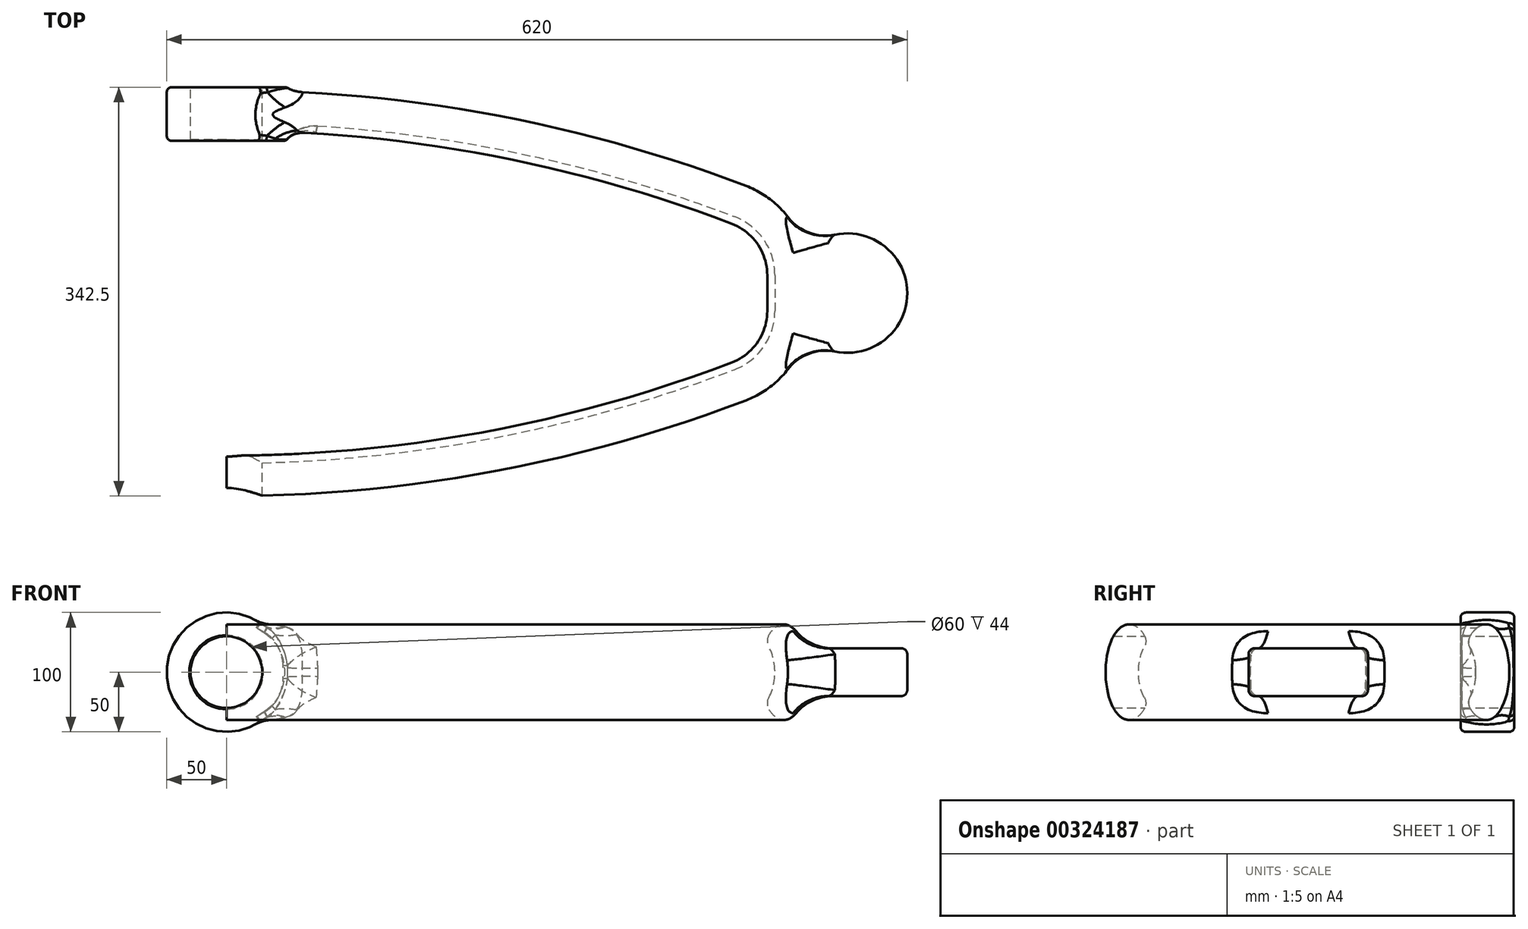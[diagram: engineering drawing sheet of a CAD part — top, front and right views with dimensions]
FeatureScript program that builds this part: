
annotation { "Feature Type Name" : "Feature", "Feature Type Description" : "" }
export const myFeature = defineFeature(function(context is Context, id is Id, definition is map)
    precondition{}
    {
        {
            var Q0;
            Q0=qCreatedBy(makeId("Top.planeOp"),FACE);
            var sketch = newSketch(context, id + "F0", { "sketchPlane" : qUnion([Q0])});
            skArc(sketch, "E0", {"start": v(28.07, 71.05) * mm, "mid": v(-182.36, 130.1) * mm, "end": v(-400, 150) * mm});
            skArc(sketch, "E1", {"start": v(66.66, 15) * mm, "mid": v(56.08, 49.03) * mm, "end": v(28.07, 71.05) * mm});
            skLineSegment(sketch, "E2", {"start": v(0, 0) * mm, "end": v(-439.5, 0) * mm, "construction": true});
            skLineSegment(sketch, "E3", {"start": v(-400, 150) * mm, "end": v(-513.06, 150) * mm, "construction": true});
            skLineSegment(sketch, "E4", {"start": v(-470.76, -150) * mm, "end": v(-400, -150) * mm, "construction": true});
            skArc(sketch, "E5", {"start": v(-400, -150) * mm, "mid": v(-182.36, -130.1) * mm, "end": v(28.07, -71.05) * mm});
            skArc(sketch, "E6", {"start": v(28.07, -71.05) * mm, "mid": v(56.08, -49.03) * mm, "end": v(66.66, -15) * mm});
            skLineSegment(sketch, "E7", {"start": v(66.66, 15) * mm, "end": v(66.66, -15) * mm});
            skLineSegment(sketch, "E8", {"start": v(66.66, 0) * mm, "end": v(0, 0) * mm});
            skSolve(sketch);
        }
        {
            var Q0;
            Q0=qCreatedBy(makeId("Right.planeOp"),FACE);
            var Q1;
            Q1=sQuery(id+"F0.wireOp",VERTEX,"E3.start");
            cPlane(context, id + "F1", {"entities" : qUnion([Q0, Q1]), "cplaneType" : CPlaneType.PLANE_POINT, "offset" : 25 * mm, "width" : 150 * mm, "height" : 150 * mm});
        }
        {
            var Q0;
            Q0=qCreatedBy(id+"F1.planeOp",FACE);
            var sketch = newSketch(context, id + "F2", { "sketchPlane" : qUnion([Q0])});
            skEllipse(sketch, "E9", {"center": v(150, 0) * mm, "majorRadius": 40 * mm, "minorRadius": 20 * mm, "majorAxis": v(0, 1)});
            skSolve(sketch);
        }
        {
            var Q0;
            Q0=makeQuery(id+"F2.imprint","IMPRINT",FACE,{"disambiguationData":[TD([[makeQuery(id+"F2.imprint","IMPRINT",EDGE,{"derivedFrom":sQuery(id+"F2.wireOp",EDGE,"E9")}),1.0]])]});
            var Q1;
            Q1=sQuery(id+"F0.wireOp",EDGE,"E0");
            var Q2;
            Q2=sQuery(id+"F0.wireOp",EDGE,"E1");
            var Q3;
            Q3=sQuery(id+"F0.wireOp",EDGE,"E7");
            var Q4;
            Q4=sQuery(id+"F0.wireOp",EDGE,"E6");
            var Q5;
            Q5=sQuery(id+"F0.wireOp",EDGE,"E5");
            sweep(context, id + "F3", {"profiles" : qUnion([Q0]), "path" : qUnion([Q1, Q2, Q3, Q4, Q5])});
        }
        {
            var Q0;
            Q0=qCreatedBy(id+"F1.planeOp",FACE);
            var sketch = newSketch(context, id + "F4", { "sketchPlane" : qUnion([Q0])});
            skEllipse(sketch, "E10", {"center": v(125, 0) * mm, "majorRadius": 30 * mm, "minorRadius": 17.5 * mm, "majorAxis": v(0, -1)});
            skSolve(sketch);
        }
        {
            var Q0;
            Q0=makeQuery(id+"F4.imprint","IMPRINT",FACE,{"disambiguationData":[TD([[makeQuery(id+"F4.imprint","IMPRINT",EDGE,{"derivedFrom":sQuery(id+"F4.wireOp",EDGE,"E10")}),1.0]])]});
            var Q1;
            Q1=sQuery(id+"F0.wireOp",EDGE,"E0");
            var Q2;
            Q2=sQuery(id+"F0.wireOp",EDGE,"E1");
            var Q3;
            Q3=sQuery(id+"F0.wireOp",EDGE,"E7");
            var Q4;
            Q4=sQuery(id+"F0.wireOp",EDGE,"E6");
            var Q5;
            Q5=sQuery(id+"F0.wireOp",EDGE,"E5");
            sweep(context, id + "F5", {"operationType" : NewBodyOperationType.REMOVE, "profiles" : qUnion([Q0]), "path" : qUnion([Q1, Q2, Q3, Q4, Q5])});
        }
        {
            var Q0;
            {var subQ0=sQuery(id+"F0.wireOp",EDGE,"E0");Q0=makeQuery(id+"F5.boolean.opBoolean","INTERSECT",EDGE,{"disambiguationData":[OD(0.0)],"derivedFrom":[makeQuery(id+"F3.opSweep","SWEPT_FACE",FACE,{"disambiguationData":[OSD([subQ0,sQuery(id+"F2.wireOp",EDGE,"E9")])]}),makeQuery(id+"F5.opSweep","SWEPT_FACE",FACE,{"disambiguationData":[OSD([subQ0,sQuery(id+"F4.wireOp",EDGE,"E10")])]})]});}
            var Q1;
            {var subQ0=sQuery(id+"F0.wireOp",EDGE,"E0");Q1=makeQuery(id+"F5.boolean.opBoolean","INTERSECT",EDGE,{"disambiguationData":[OD(1.0)],"derivedFrom":[makeQuery(id+"F3.opSweep","SWEPT_FACE",FACE,{"disambiguationData":[OSD([subQ0,sQuery(id+"F2.wireOp",EDGE,"E9")])]}),makeQuery(id+"F5.opSweep","SWEPT_FACE",FACE,{"disambiguationData":[OSD([subQ0,sQuery(id+"F4.wireOp",EDGE,"E10")])]})]});}
            fillet(context, id + "F6", {"entities" : qUnion([Q0, Q1]), "radius" : 10 * mm, "tangentPropagation" : true, "allowEdgeOverflow" : false});
        }
        {
            var Q0;
            Q0=sQuery(id+"F2.wireOp",VERTEX,"E9.center");
            var Q1;
            Q1=qCreatedBy(makeId("Front.planeOp"),FACE);
            cPlane(context, id + "F7", {"entities" : qUnion([Q0, Q1]), "cplaneType" : CPlaneType.PLANE_POINT, "offset" : 25 * mm, "width" : 150 * mm, "height" : 150 * mm});
        }
        {
            var Q0;
            Q0=qCreatedBy(id+"F7.planeOp",FACE);
            var sketch = newSketch(context, id + "F8", { "sketchPlane" : qUnion([Q0])});
            skCircle(sketch, "E11", {"center": v(-400, 0) * mm, "radius": 50 * mm});
            skSolve(sketch);
        }
        {
            var Q0;
            Q0=makeQuery(id+"F8.imprint","IMPRINT",FACE,{"disambiguationData":[TD([[makeQuery(id+"F8.imprint","IMPRINT",EDGE,{"derivedFrom":sQuery(id+"F8.wireOp",EDGE,"E11")}),1.0]])]});
            extrude(context, id + "F9", {"entities" : qUnion([Q0]), "operationType" : NewBodyOperationType.ADD, "depth" : 45 * mm, "symmetric" : true});
        }
        {
            var Q0;
            Q0=makeQuery(id+"F9.boolean.opBoolean","INTERSECT",EDGE,{"derivedFrom":[makeQuery(id+"F3.opSweep","SWEPT_FACE",FACE,{"disambiguationData":[OSD([sQuery(id+"F0.wireOp",EDGE,"E0"),sQuery(id+"F2.wireOp",EDGE,"E9")])]}),makeQuery(id+"F9.opExtrude","SWEPT_FACE",FACE,{"disambiguationData":[OSD([sQuery(id+"F8.wireOp",EDGE,"E11")])]})]});
            fillet(context, id + "F10", {"entities" : qUnion([Q0]), "radius" : 30 * mm, "tangentPropagation" : true, "allowEdgeOverflow" : false});
        }
        {
            var Q0;
            {var subQ0=sQuery(id+"F8.wireOp",EDGE,"E11");Q0=makeQuery(id+"F10.opFillet","BLEND_EDGE",EDGE,{"disambiguationData":[OD(0.0)],"blendedFrom":[makeQuery(id+"F9.boolean.opBoolean","INTERSECT",EDGE,{"derivedFrom":[makeQuery(id+"F3.opSweep","SWEPT_FACE",FACE,{"disambiguationData":[OSD([sQuery(id+"F0.wireOp",EDGE,"E0"),sQuery(id+"F2.wireOp",EDGE,"E9")])]}),makeQuery(id+"F9.opExtrude","SWEPT_FACE",FACE,{"disambiguationData":[OSD([subQ0])]})]}),makeQuery(id+"F9.opExtrude","CAP_FACE",FACE,{"disambiguationData":[OSD([subQ0])],"isStart":false})],"blendedInto":[makeQuery(id+"F9.opExtrude","CAP_FACE",FACE,{"disambiguationData":[OSD([subQ0])],"isStart":false})]});}
            var Q1;
            {var subQ0=sQuery(id+"F8.wireOp",EDGE,"E11");Q1=makeQuery(id+"F10.opFillet","BLEND_EDGE",EDGE,{"blendedFrom":[makeQuery(id+"F9.boolean.opBoolean","INTERSECT",EDGE,{"derivedFrom":[makeQuery(id+"F3.opSweep","SWEPT_FACE",FACE,{"disambiguationData":[OSD([sQuery(id+"F0.wireOp",EDGE,"E0"),sQuery(id+"F2.wireOp",EDGE,"E9")])]}),makeQuery(id+"F9.opExtrude","SWEPT_FACE",FACE,{"disambiguationData":[OSD([subQ0])]})]}),makeQuery(id+"F9.opExtrude","CAP_FACE",FACE,{"disambiguationData":[OSD([subQ0])],"isStart":true})],"blendedInto":[makeQuery(id+"F9.opExtrude","CAP_FACE",FACE,{"disambiguationData":[OSD([subQ0])],"isStart":true})]});}
            var Q2;
            Q2=makeQuery(id+"F9.opExtrude","CAP_EDGE",EDGE,{"disambiguationData":[OSD([sQuery(id+"F8.wireOp",EDGE,"E11")])],"isStart":true});
            var Q3;
            {var subQ0=sQuery(id+"F8.wireOp",EDGE,"E11");Q3=makeQuery(id+"F10.opFillet","BLEND_EDGE",EDGE,{"disambiguationData":[OD(3.0)],"blendedFrom":[makeQuery(id+"F9.boolean.opBoolean","INTERSECT",EDGE,{"derivedFrom":[makeQuery(id+"F3.opSweep","SWEPT_FACE",FACE,{"disambiguationData":[OSD([sQuery(id+"F0.wireOp",EDGE,"E0"),sQuery(id+"F2.wireOp",EDGE,"E9")])]}),makeQuery(id+"F9.opExtrude","SWEPT_FACE",FACE,{"disambiguationData":[OSD([subQ0])]})]}),makeQuery(id+"F9.opExtrude","CAP_FACE",FACE,{"disambiguationData":[OSD([subQ0])],"isStart":false})],"blendedInto":[makeQuery(id+"F9.opExtrude","CAP_FACE",FACE,{"disambiguationData":[OSD([subQ0])],"isStart":false})]});}
            var Q4;
            Q4=makeQuery(id+"F9.opExtrude","CAP_EDGE",EDGE,{"disambiguationData":[OSD([sQuery(id+"F8.wireOp",EDGE,"E11")])],"isStart":false});
            var Q5;
            {var subQ0=sQuery(id+"F8.wireOp",EDGE,"E11");Q5=makeQuery(id+"F10.opFillet","BLEND_EDGE",EDGE,{"disambiguationData":[OD(4.0)],"blendedFrom":[makeQuery(id+"F9.boolean.opBoolean","INTERSECT",EDGE,{"derivedFrom":[makeQuery(id+"F3.opSweep","SWEPT_FACE",FACE,{"disambiguationData":[OSD([sQuery(id+"F0.wireOp",EDGE,"E0"),sQuery(id+"F2.wireOp",EDGE,"E9")])]}),makeQuery(id+"F9.opExtrude","SWEPT_FACE",FACE,{"disambiguationData":[OSD([subQ0])]})]}),makeQuery(id+"F9.opExtrude","CAP_FACE",FACE,{"disambiguationData":[OSD([subQ0])],"isStart":false})],"blendedInto":[makeQuery(id+"F9.opExtrude","CAP_FACE",FACE,{"disambiguationData":[OSD([subQ0])],"isStart":false})]});}
            var Q6;
            {var subQ0=sQuery(id+"F8.wireOp",EDGE,"E11");Q6=makeQuery(id+"F10.opFillet","BLEND_EDGE",EDGE,{"disambiguationData":[OD(2.0)],"blendedFrom":[makeQuery(id+"F9.boolean.opBoolean","INTERSECT",EDGE,{"derivedFrom":[makeQuery(id+"F3.opSweep","SWEPT_FACE",FACE,{"disambiguationData":[OSD([sQuery(id+"F0.wireOp",EDGE,"E0"),sQuery(id+"F2.wireOp",EDGE,"E9")])]}),makeQuery(id+"F9.opExtrude","SWEPT_FACE",FACE,{"disambiguationData":[OSD([subQ0])]})]}),makeQuery(id+"F9.opExtrude","CAP_FACE",FACE,{"disambiguationData":[OSD([subQ0])],"isStart":false})],"blendedInto":[makeQuery(id+"F9.opExtrude","CAP_FACE",FACE,{"disambiguationData":[OSD([subQ0])],"isStart":false})]});}
            fillet(context, id + "F11", {"entities" : qUnion([Q0, Q1, Q2, Q3, Q4, Q5, Q6]), "radius" : 5 * mm, "tangentPropagation" : true, "rho" : 0.5, "crossSection" : FilletCrossSection.CONIC, "allowEdgeOverflow" : false});
        }
        {
            var Q0;
            Q0=makeQuery(id+"F9.opExtrude","CAP_FACE",FACE,{"disambiguationData":[OSD([sQuery(id+"F8.wireOp",EDGE,"E11")])],"isStart":true});
            var sketch = newSketch(context, id + "F12", { "sketchPlane" : qUnion([Q0])});
            skCircle(sketch, "E12", {"center": v(400, 0) * mm, "radius": 30 * mm});
            skSolve(sketch);
        }
        {
            var Q0;
            Q0=makeQuery(id+"F12.imprint","IMPRINT",FACE,{"disambiguationData":[TD([[makeQuery(id+"F12.imprint","IMPRINT",EDGE,{"derivedFrom":sQuery(id+"F12.wireOp",EDGE,"E12")}),1.0]])]});
            extrude(context, id + "F13", {"entities" : qUnion([Q0]), "operationType" : NewBodyOperationType.REMOVE, "endBound" : BoundingType.THROUGH_ALL, "oppositeDirection" : true, "depth" : 25 * mm});
        }
        {
            var Q0;
            Q0=qCreatedBy(makeId("Top.planeOp"),FACE);
            var sketch = newSketch(context, id + "F14", { "sketchPlane" : qUnion([Q0])});
            skCircle(sketch, "E13", {"center": v(120, 0) * mm, "radius": 50 * mm});
            skSolve(sketch);
        }
        {
            var Q0;
            Q0=makeQuery(id+"F14.imprint","IMPRINT",FACE,{"disambiguationData":[TD([[makeQuery(id+"F14.imprint","IMPRINT",EDGE,{"derivedFrom":sQuery(id+"F14.wireOp",EDGE,"E13")}),1.0]])]});
            extrude(context, id + "F15", {"entities" : qUnion([Q0]), "operationType" : NewBodyOperationType.ADD, "depth" : 40 * mm, "symmetric" : true});
        }
        {
            var Q0;
            Q0=makeQuery(id+"F15.opExtrude","CAP_EDGE",EDGE,{"disambiguationData":[OSD([sQuery(id+"F14.wireOp",EDGE,"E13")])],"isStart":true});
            var Q1;
            Q1=makeQuery(id+"F15.opExtrude","CAP_EDGE",EDGE,{"disambiguationData":[OSD([sQuery(id+"F14.wireOp",EDGE,"E13")])],"isStart":false});
            fillet(context, id + "F16", {"entities" : qUnion([Q0, Q1]), "radius" : 5 * mm, "tangentPropagation" : true, "allowEdgeOverflow" : false});
        }
        {
            var Q0;
            Q0=makeQuery(id+"F15.boolean.opBoolean","INTERSECT",EDGE,{"derivedFrom":[makeQuery(id+"F3.opSweep","SWEPT_FACE",FACE,{"disambiguationData":[OSD([sQuery(id+"F0.wireOp",EDGE,"E7"),sQuery(id+"F2.wireOp",EDGE,"E9")])]}),makeQuery(id+"F15.opExtrude","CAP_FACE",FACE,{"disambiguationData":[OSD([sQuery(id+"F14.wireOp",EDGE,"E13")])],"isStart":true})]});
            fillet(context, id + "F17", {"entities" : qUnion([Q0]), "radius" : 40 * mm, "tangentPropagation" : true, "allowEdgeOverflow" : false});
        }
        {
            var Q0;
            Q0=makeQuery(id+"F13.boolean.opBoolean","COPY",EDGE,{"derivedFrom":makeQuery(id+"F13.opExtrude","CAP_EDGE",EDGE,{"disambiguationData":[OSD([sQuery(id+"F12.wireOp",EDGE,"E12")])],"isStart":true})});
            var Q1;
            Q1=makeQuery(id+"F13.boolean.opBoolean","INTERSECT",EDGE,{"derivedFrom":[makeQuery(id+"F9.opExtrude","CAP_FACE",FACE,{"disambiguationData":[OSD([sQuery(id+"F8.wireOp",EDGE,"E11")])],"isStart":false}),makeQuery(id+"F13.opExtrude","SWEPT_FACE",FACE,{"disambiguationData":[OSD([sQuery(id+"F12.wireOp",EDGE,"E12")])]})]});
            var Q2;
            Q2=makeQuery(id+"F13.boolean.opBoolean","INTERSECT",EDGE,{"derivedFrom":[makeQuery(id+"FcmCyu5l10xMOln_1.1.F9.opExtrude","CAP_FACE",FACE,{"disambiguationData":[OSD([sQuery(id+"F8.wireOp",EDGE,"E11")])],"isStart":false}),makeQuery(id+"F13.opExtrude","SWEPT_FACE",FACE,{"disambiguationData":[OSD([sQuery(id+"F12.wireOp",EDGE,"E12")])]})]});
            var Q3;
            Q3=makeQuery(id+"F13.boolean.opBoolean","INTERSECT",EDGE,{"derivedFrom":[makeQuery(id+"FcmCyu5l10xMOln_1.1.F9.opExtrude","CAP_FACE",FACE,{"disambiguationData":[OSD([sQuery(id+"F8.wireOp",EDGE,"E11")])],"isStart":true}),makeQuery(id+"F13.opExtrude","SWEPT_FACE",FACE,{"disambiguationData":[OSD([sQuery(id+"F12.wireOp",EDGE,"E12")])]})]});
            chamfer(context, id + "F18", {"entities" : qUnion([Q0, Q1, Q2, Q3]), "width" : 1 * mm, "tangentPropagation" : true});
        }
    });
